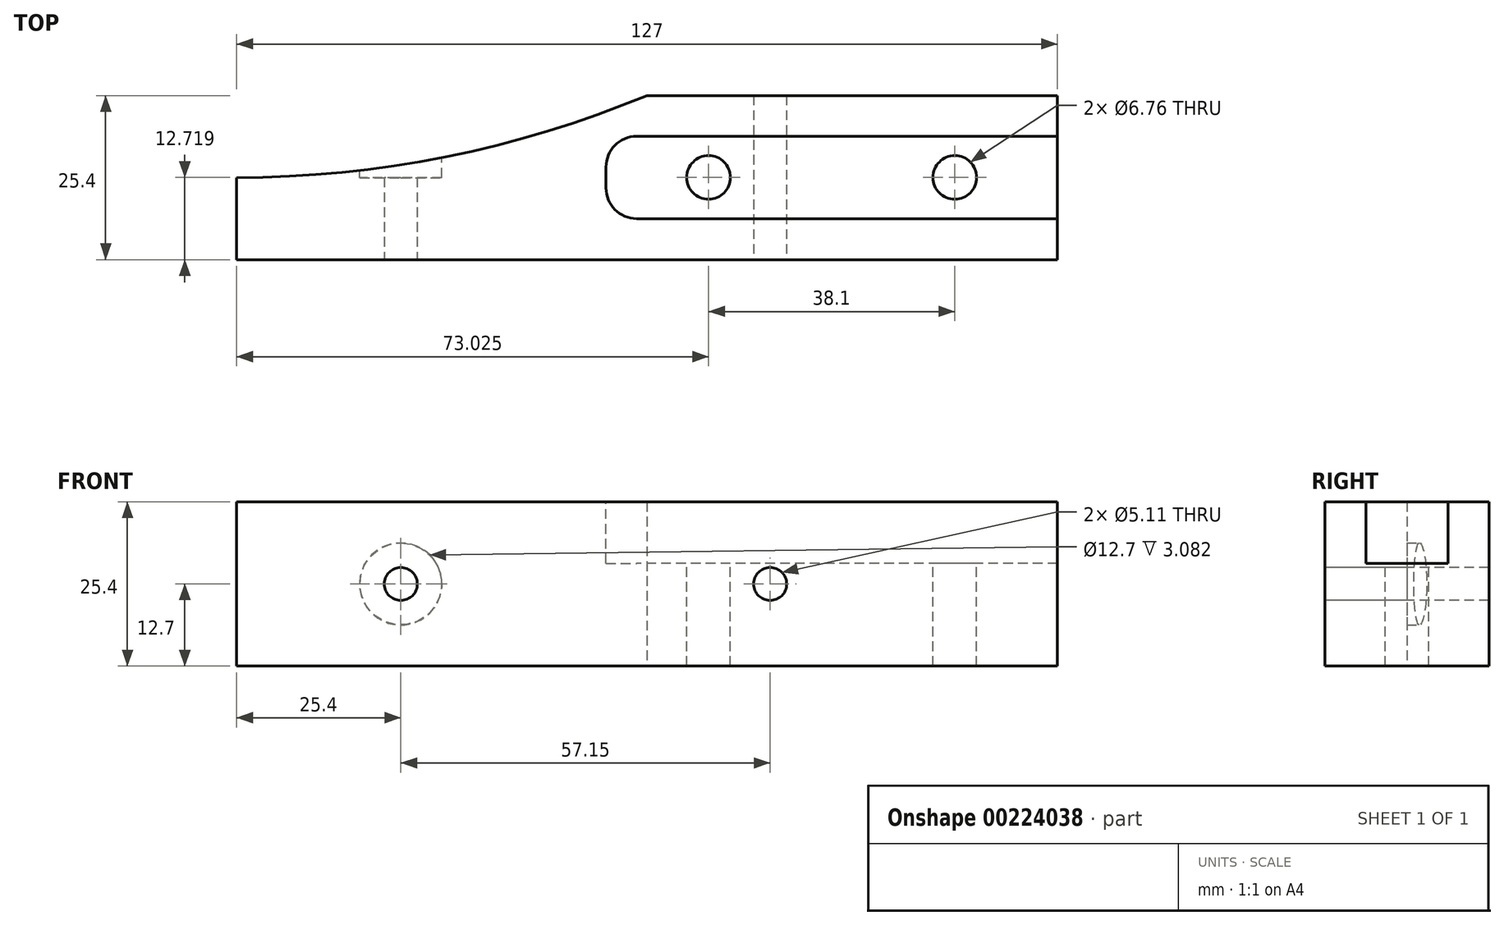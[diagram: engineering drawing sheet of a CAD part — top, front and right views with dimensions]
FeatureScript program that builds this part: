
annotation { "Feature Type Name" : "Feature", "Feature Type Description" : "" }
export const myFeature = defineFeature(function(context is Context, id is Id, definition is map)
    precondition{}
    {
        {
            var Q0;
            Q0=qCreatedBy(makeId("Top.planeOp"),FACE);
            var sketch = newSketch(context, id + "F0", { "sketchPlane" : qUnion([Q0])});
            skLineSegment(sketch, "E0", {"start": v(0, 0) * mm, "end": v(127, 0) * mm});
            skLineSegment(sketch, "E1", {"start": v(127, 0) * mm, "end": v(127, 25.4) * mm});
            skLineSegment(sketch, "E2", {"start": v(127, 25.4) * mm, "end": v(63.5, 25.4) * mm});
            skArc(sketch, "E3", {"start": v(0, 12.7) * mm, "mid": v(32.38, 15.9) * mm, "end": v(63.5, 25.4) * mm});
            skLineSegment(sketch, "E4", {"start": v(0, 0) * mm, "end": v(0, 12.7) * mm});
            skSolve(sketch);
        }
        {
            var Q0;
            Q0 = qSketchRegion(id + "F0", true);
            extrude(context, id + "F1", {"entities" : qUnion([Q0]), "depth" : 25.4 * mm});
        }
        {
            var Q0;
            Q0=makeQuery(id+"F1.opExtrude","SWEPT_FACE",FACE,{"disambiguationData":[OSD([sQuery(id+"F0.wireOp",EDGE,"E0")])]});
            var sketch = newSketch(context, id + "F2", { "sketchPlane" : qUnion([Q0])});
            skPoint(sketch, "E5", {"position": v(82.55, 12.7) * mm});
            skPoint(sketch, "E6", {"position": v(25.4, 12.7) * mm});
            skSolve(sketch);
        }
        {
            var Q0;
            Q0=sQuery(id+"F2.wireOp",VERTEX,"E6");
            var Q1;
            Q1=sQuery(id+"F2.wireOp",VERTEX,"E5");
            var Q2;
            Q2=makeQuery(id+"F1.opExtrude","SWEPT_BODY",BODY,{"disambiguationData":[OSD([sQuery(id+"F0.wireOp",EDGE,"E0"),sQuery(id+"F0.wireOp",EDGE,"E1"),sQuery(id+"F0.wireOp",EDGE,"VCfkEBET-YDmr-PedA-DVFU-kMfEjuCusRZ9"),sQuery(id+"F0.wireOp",EDGE,"z4dKKlDq-vNw7-ikJk-eWWa-dQcs3N2Cca5n"),sQuery(id+"F0.wireOp",EDGE,"eR8jCO09-kB8t-xtmB-KxQ9-8UpsDd1UJrAj"),sQuery(id+"F0.wireOp",EDGE,"qdVimR2G-YRAf-2E0D-RULz-ZDdSM2E4mXBj"),sQuery(id+"F0.wireOp",EDGE,"E2"),sQuery(id+"F0.wireOp",EDGE,"E3"),sQuery(id+"F0.wireOp",EDGE,"E4")])]});
            hole(context, id + "F3", {"style" : HoleStyle.SIMPLE, "endStyle" : HoleEndStyle.THROUGH, "standardTappedOrClearance" : lookupTablePath({ "standard" : "ANSI", "fit" : "Normal (ASME)", "size" : "#10", "type" : "Clearance" }), "standardBlindInLast" : lookupTablePath({ "fit" : "Free", "standard" : "ANSI", "size" : "#10", "type" : "Clearance" }), "holeDiameter" : 5.1 * mm, "locations" : qUnion([Q0, Q1]), "scope" : qUnion([Q2]), "isTappedThrough" : true});
        }
        {
            var Q0;
            Q0=makeQuery(id+"F1.opExtrude","SWEPT_FACE",FACE,{"disambiguationData":[OSD([sQuery(id+"F0.wireOp",EDGE,"E2")])]});
            var sketch = newSketch(context, id + "F4", { "sketchPlane" : qUnion([Q0])});
            skCircle(sketch, "E7", {"center": v(-25.4, 12.7) * mm, "radius": 6.35 * mm});
            skSolve(sketch);
        }
        {
            var Q0;
            Q0 = qSketchRegion(id + "F4", true);
            extrude(context, id + "F5", {"entities" : qUnion([Q0]), "operationType" : NewBodyOperationType.REMOVE, "oppositeDirection" : true, "depth" : 12.7 * mm});
        }
        {
            var Q0;
            Q0=makeQuery(id+"F1.opExtrude","CAP_FACE",FACE,{"disambiguationData":[OSD([sQuery(id+"F0.wireOp",EDGE,"E0"),sQuery(id+"F0.wireOp",EDGE,"E1"),sQuery(id+"F0.wireOp",EDGE,"E2"),sQuery(id+"F0.wireOp",EDGE,"E3"),sQuery(id+"F0.wireOp",EDGE,"E4")])],"isStart":false});
            var sketch = newSketch(context, id + "F6", { "sketchPlane" : qUnion([Q0])});
            skLineSegment(sketch, "E8.bottom", {"start": v(127, 6.35) * mm, "end": v(57.15, 6.35) * mm});
            skLineSegment(sketch, "E8.top", {"start": v(127, 19.09) * mm, "end": v(57.15, 19.09) * mm});
            skLineSegment(sketch, "E8.left", {"start": v(127, 6.35) * mm, "end": v(127, 19.09) * mm});
            skLineSegment(sketch, "E8.right", {"start": v(57.15, 6.35) * mm, "end": v(57.15, 19.09) * mm});
            skSolve(sketch);
        }
        {
            var Q0;
            Q0 = qSketchRegion(id + "F6", true);
            extrude(context, id + "F7", {"entities" : qUnion([Q0]), "operationType" : NewBodyOperationType.REMOVE, "oppositeDirection" : true, "depth" : 9.52 * mm});
        }
        {
            var Q0;
            Q0=makeQuery(id+"F1.opExtrude","CAP_FACE",FACE,{"disambiguationData":[OSD([sQuery(id+"F0.wireOp",EDGE,"E0"),sQuery(id+"F0.wireOp",EDGE,"E1"),sQuery(id+"F0.wireOp",EDGE,"E2"),sQuery(id+"F0.wireOp",EDGE,"E3"),sQuery(id+"F0.wireOp",EDGE,"E4")])],"isStart":false});
            var sketch = newSketch(context, id + "F8", { "sketchPlane" : qUnion([Q0])});
            skPoint(sketch, "E9", {"position": v(73.03, 12.72) * mm});
            skPoint(sketch, "E10", {"position": v(111.12, 12.72) * mm});
            skSolve(sketch);
        }
        {
            var Q0;
            Q0=sQuery(id+"F8.wireOp",VERTEX,"E9");
            var Q1;
            Q1=sQuery(id+"F8.wireOp",VERTEX,"E10");
            var Q2;
            Q2=makeQuery(id+"F1.opExtrude","SWEPT_BODY",BODY,{"disambiguationData":[OSD([sQuery(id+"F0.wireOp",EDGE,"E0"),sQuery(id+"F0.wireOp",EDGE,"E1"),sQuery(id+"F0.wireOp",EDGE,"E2"),sQuery(id+"F0.wireOp",EDGE,"E3"),sQuery(id+"F0.wireOp",EDGE,"E4")])]});
            hole(context, id + "F9", {"style" : HoleStyle.SIMPLE, "endStyle" : HoleEndStyle.THROUGH, "standardTappedOrClearance" : lookupTablePath({ "standard" : "ANSI", "fit" : "Normal (ASME)", "size" : "1/4", "type" : "Clearance" }), "standardBlindInLast" : lookupTablePath({ "fit" : "Free", "standard" : "ANSI", "size" : "1/4", "type" : "Clearance" }), "holeDiameter" : 6.76 * mm, "locations" : qUnion([Q0, Q1]), "scope" : qUnion([Q2]), "isTappedThrough" : true});
        }
        {
            var Q0;
            Q0=makeQuery(id+"F7.boolean.opBoolean","COPY",EDGE,{"derivedFrom":makeQuery(id+"F7.opExtrude","SWEPT_EDGE",EDGE,{"disambiguationData":[OSD([sQuery(id+"F6.wireOp",EDGE,"E8.top"),sQuery(id+"F6.wireOp",EDGE,"E8.right")])]})});
            var Q1;
            Q1=makeQuery(id+"F7.boolean.opBoolean","COPY",EDGE,{"derivedFrom":makeQuery(id+"F7.opExtrude","SWEPT_EDGE",EDGE,{"disambiguationData":[OSD([sQuery(id+"F6.wireOp",EDGE,"E8.bottom"),sQuery(id+"F6.wireOp",EDGE,"E8.right")])]})});
            fillet(context, id + "F10", {"entities" : qUnion([Q0, Q1]), "radius" : 4.76 * mm, "tangentPropagation" : true, "allowEdgeOverflow" : false});
        }
    });
